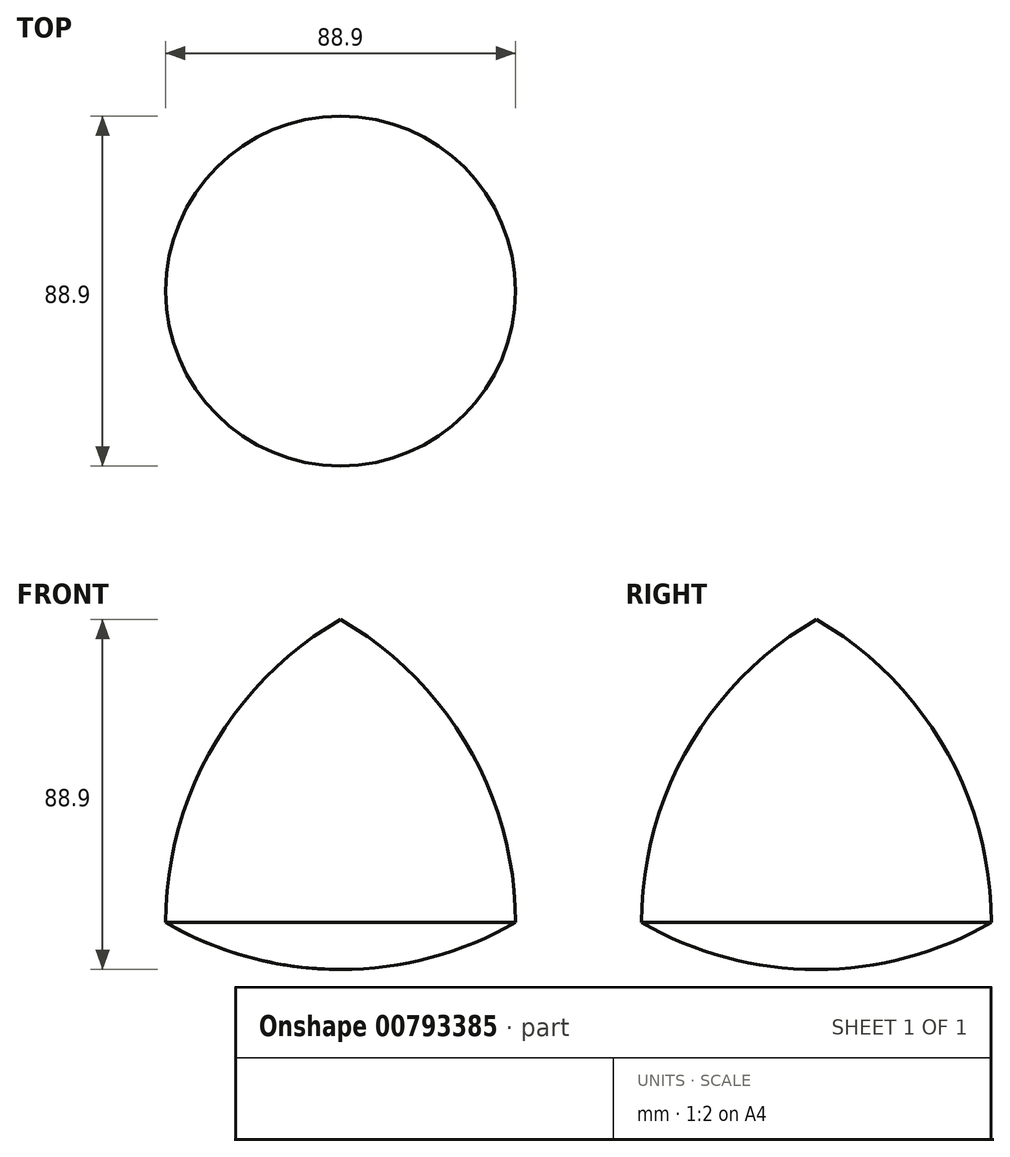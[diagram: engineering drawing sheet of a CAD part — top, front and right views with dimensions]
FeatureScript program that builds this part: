
annotation { "Feature Type Name" : "Feature", "Feature Type Description" : "" }
export const myFeature = defineFeature(function(context is Context, id is Id, definition is map)
    precondition{}
    {
        {
            var Q0;
            Q0=qCreatedBy(makeId("Front.planeOp"),FACE);
            var sketch = newSketch(context, id + "F0", { "sketchPlane" : qUnion([Q0])});
            skArc(sketch, "E0", {"start": v(-44.45, 11.91) * mm, "mid": v(-23, 3.03) * mm, "end": v(0, 0) * mm});
            skArc(sketch, "E1", {"start": v(0, 88.9) * mm, "mid": v(-32.54, 56.36) * mm, "end": v(-44.45, 11.91) * mm});
            skLineSegment(sketch, "E2", {"start": v(0, 88.9) * mm, "end": v(0, 0) * mm});
            skSolve(sketch);
        }
        {
            var Q0;
            Q0=makeQuery(id+"F0.imprint","IMPRINT",FACE,{"disambiguationData":[TD([[makeQuery(id+"F0.imprint","IMPRINT",EDGE,{"derivedFrom":sQuery(id+"F0.wireOp",EDGE,"E0")}),1.0]])]});
            var Q1;
            Q1=sQuery(id+"F0.wireOp",EDGE,"E2");
            revolve(context, id + "F1", {"surfaceOperationType" : NewSurfaceOperationType.NEW, "entities" : qUnion([Q0]), "axis" : qUnion([Q1]), "revolveType" : RevolveType.FULL});
        }
    });
